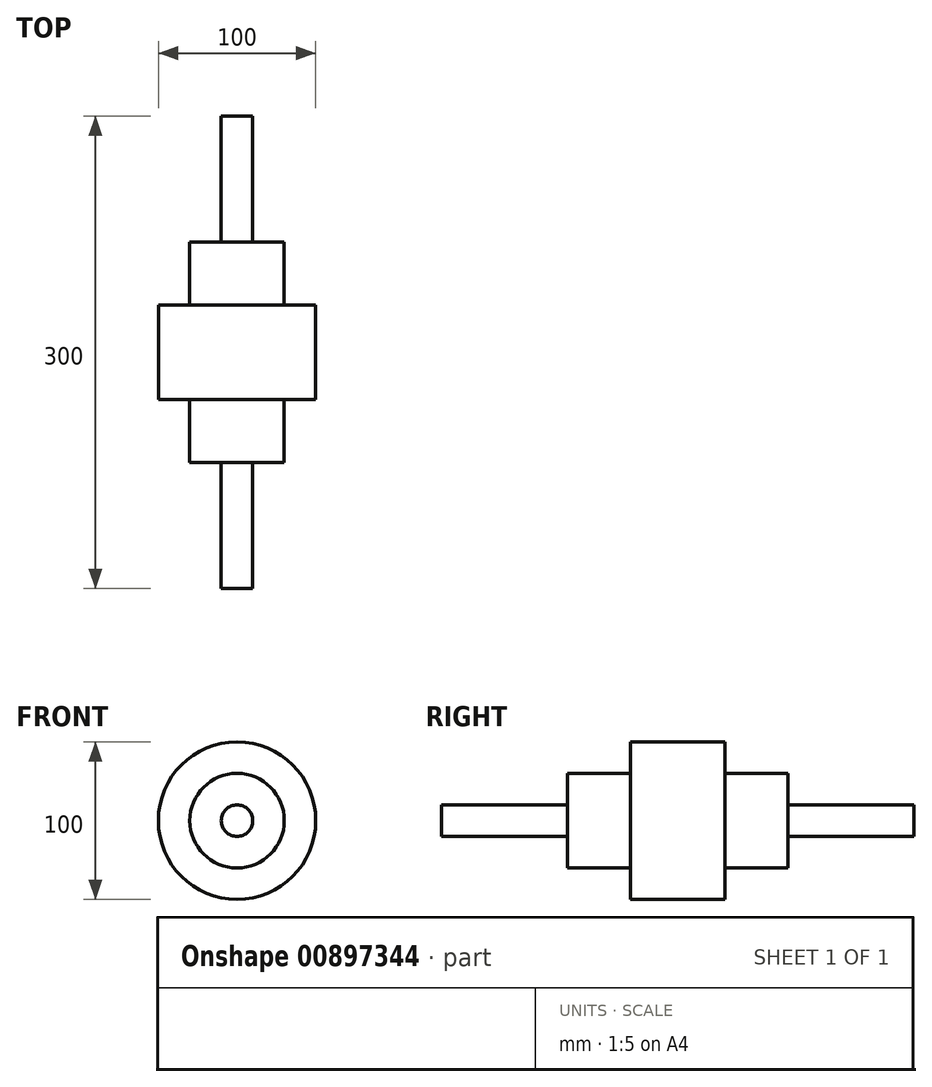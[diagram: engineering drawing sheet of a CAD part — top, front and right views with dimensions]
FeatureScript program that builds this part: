
annotation { "Feature Type Name" : "Feature", "Feature Type Description" : "" }
export const myFeature = defineFeature(function(context is Context, id is Id, definition is map)
    precondition{}
    {
        {
            var Q0;
            Q0=qCreatedBy(makeId("Front.planeOp"),FACE);
            var sketch = newSketch(context, id + "F0", { "sketchPlane" : qUnion([Q0])});
            skCircle(sketch, "E0", {"center": v(0, 0) * mm, "radius": 50 * mm});
            skCircle(sketch, "E1", {"center": v(0, 0) * mm, "radius": 20 * mm});
            skSolve(sketch);
        }
        {
            var Q0;
            Q0=makeQuery(id+"F0.imprint","IMPRINT",FACE,{"disambiguationData":[TD([[makeQuery(id+"F0.imprint","IMPRINT",EDGE,{"derivedFrom":sQuery(id+"F0.wireOp",EDGE,"E0")}),1.0]])]});
            var Q1;
            Q1=makeQuery(id+"F0.imprint","IMPRINT",FACE,{"disambiguationData":[TD([[makeQuery(id+"F0.imprint","IMPRINT",EDGE,{"derivedFrom":sQuery(id+"F0.wireOp",EDGE,"E1")}),1.0]])]});
            extrude(context, id + "F1", {"entities" : qUnion([Q0, Q1]), "depth" : 60 * mm, "offsetDistance" : 25.4 * mm});
        }
        {
            var Q0;
            Q0=makeQuery(id+"F1.opExtrude","CAP_FACE",FACE,{"disambiguationData":[OSD([sQuery(id+"F0.wireOp",EDGE,"E0")])],"isStart":false});
            var sketch = newSketch(context, id + "F2", { "sketchPlane" : qUnion([Q0])});
            skCircle(sketch, "E2", {"center": v(0, 0) * mm, "radius": 30 * mm});
            skSolve(sketch);
        }
        {
            var Q0;
            Q0=makeQuery(id+"F2.imprint","IMPRINT",FACE,{"disambiguationData":[TD([[makeQuery(id+"F2.imprint","IMPRINT",EDGE,{"derivedFrom":sQuery(id+"F2.wireOp",EDGE,"E2")}),1.0]])]});
            extrude(context, id + "F3", {"entities" : qUnion([Q0]), "operationType" : NewBodyOperationType.ADD, "depth" : 40 * mm, "offsetDistance" : 25.4 * mm});
        }
        {
            var Q0;
            Q0=makeQuery(id+"F3.opExtrude","CAP_FACE",FACE,{"disambiguationData":[OSD([sQuery(id+"F2.wireOp",EDGE,"E2")])],"isStart":false});
            var sketch = newSketch(context, id + "F4", { "sketchPlane" : qUnion([Q0])});
            skCircle(sketch, "E3", {"center": v(0, 0) * mm, "radius": 10 * mm});
            skSolve(sketch);
        }
        {
            var Q0;
            Q0=makeQuery(id+"F4.imprint","IMPRINT",FACE,{"disambiguationData":[TD([[makeQuery(id+"F4.imprint","IMPRINT",EDGE,{"derivedFrom":sQuery(id+"F4.wireOp",EDGE,"E3")}),1.0]])]});
            extrude(context, id + "F5", {"entities" : qUnion([Q0]), "operationType" : NewBodyOperationType.ADD, "depth" : 80 * mm, "offsetDistance" : 25.4 * mm});
        }
        {
            var Q0;
            Q0=makeQuery(id+"F1.opExtrude","CAP_FACE",FACE,{"disambiguationData":[OSD([sQuery(id+"F0.wireOp",EDGE,"E0")])],"isStart":true});
            var sketch = newSketch(context, id + "F6", { "sketchPlane" : qUnion([Q0])});
            skCircle(sketch, "E4", {"center": v(0, 0) * mm, "radius": 30 * mm});
            skSolve(sketch);
        }
        {
            var Q0;
            Q0=makeQuery(id+"F6.imprint","IMPRINT",FACE,{"disambiguationData":[TD([[makeQuery(id+"F6.imprint","IMPRINT",EDGE,{"derivedFrom":sQuery(id+"F6.wireOp",EDGE,"E4")}),1.0]])]});
            extrude(context, id + "F7", {"entities" : qUnion([Q0]), "operationType" : NewBodyOperationType.ADD, "depth" : 40 * mm, "offsetDistance" : 25.4 * mm});
        }
        {
            var Q0;
            Q0=makeQuery(id+"F7.opExtrude","CAP_FACE",FACE,{"disambiguationData":[OSD([sQuery(id+"F6.wireOp",EDGE,"E4")])],"isStart":false});
            var sketch = newSketch(context, id + "F8", { "sketchPlane" : qUnion([Q0])});
            skCircle(sketch, "E5", {"center": v(0, 0) * mm, "radius": 10 * mm});
            skSolve(sketch);
        }
        {
            var Q0;
            Q0=makeQuery(id+"F8.imprint","IMPRINT",FACE,{"disambiguationData":[TD([[makeQuery(id+"F8.imprint","IMPRINT",EDGE,{"derivedFrom":sQuery(id+"F8.wireOp",EDGE,"E5")}),1.0]])]});
            extrude(context, id + "F9", {"entities" : qUnion([Q0]), "operationType" : NewBodyOperationType.ADD, "depth" : 80 * mm, "offsetDistance" : 25.4 * mm});
        }
    });
